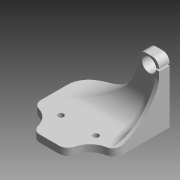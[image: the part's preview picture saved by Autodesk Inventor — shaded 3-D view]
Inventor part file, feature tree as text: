
AUTODESK INVENTOR PART (.ipt)
format: ipt  version: 2015 SP1 (Build 190203100, 203)  size: 284,160 bytes
history: native  units: mm
features: extrude x9, sketch x9, fillet x6, projected_geometry x5, reference x5, hole x2
ambient origin geometry x8: Origin, YZ Plane, XZ Plane, XY Plane, X Axis, Y Axis, Z Axis, Center Point
bodies: Body1 (feature_tree)
feature tree (36):
  extrude  "back plate Extrusion2"  Depth=18.0mm
  extrude  "Extrusion3"  Depth=4.0mm
  extrude  "Extrusion6"  Depth=8.0mm
  extrude  "Extrusion7"  Depth=11.5mm TaperAngle=0.0deg
  hole  "Hole4"  [1 undecoded]
  extrude  "Extrusion8"  Depth=20.35mm
  extrude  "Extrusion9"  Depth=1.0mm
  fillet  "Fillet4"  Radius=6.0mm
  extrude  "Extrusion10"  Depth=15.85mm TaperAngle=0.0deg
  extrude  "Extrusion12"  Depth=4.0mm
  extrude  "Extrusion13"  Depth=5.0mm TaperAngle=0.0deg
  fillet  "Fillet13"  Radius=5.25mm
  fillet  "Fillet14"  Radius=30.0mm
  fillet  "Fillet15"  Radius=2.0mm
  fillet  "Fillet16"  Radius=30.0mm
  fillet  "Fillet17"  Radius=13.0mm
  hole  "Hole5"  [1 undecoded]
  sketch  "Sketch4"  dims[d21=4.0mm d22=0.0mm d31=18.0mm]
  projected_geometry  "Projected Loop1"
  sketch  "Sketch9"  dims[d32=4.0mm d33=4.0mm]
  reference  "Reference1"
  reference  "Reference2"
  sketch  "Sketch11"  dims[d34=17.0mm d35=8.0mm]
  reference  "Reference3"
  sketch  "Sketch12"  dims[d36=8.0mm d44=11.5mm d45=0.0mm]
  sketch  "Sketch13"  dims[d58=4.0mm d59=6.0mm d60=0.0mm]
  projected_geometry  "Projected Loop2"
  sketch  "Sketch14"  dims[d63=5.5mm d64=20.35mm]
  projected_geometry  "Projected Loop3"
  sketch  "Sketch16"  dims[d65=6.0mm d66=0.0mm]
  projected_geometry  "Projected Loop5"
  sketch  "Sketch17"  dims[d67=8.0mm d68=6.0mm d69=4.0mm d70=2.0mm d71=90.0deg d72=8.0mm d73=20.594885mm d74=1.0mm d75=6.0mm]
  projected_geometry  "Projected Loop6"
  sketch  "Sketch19"  dims[d76=6.0mm d77=0.0mm d78=15.85mm d79=0.0mm d80=4.0mm d85=5.0mm d86=0.0mm d94=5.25mm d95=0.0mm d96=30.0mm d97=2.0mm d98=0.0mm d101=30.0mm d102=13.0mm d103=12.0mm d104=5.0mm d105=7.0mm d106=3.2mm d107=6.0mm d108=4.0mm d109=2.0mm d110=90.0deg d111=8.0mm d112=20.594885mm]
  reference  "Reference4"
  reference  "Reference5"
note: 2 required parameter values undecoded (feature->parameter linkage not recoverable at this tier; creation-order binding heuristic only, values carry confidence <= 0.55)
